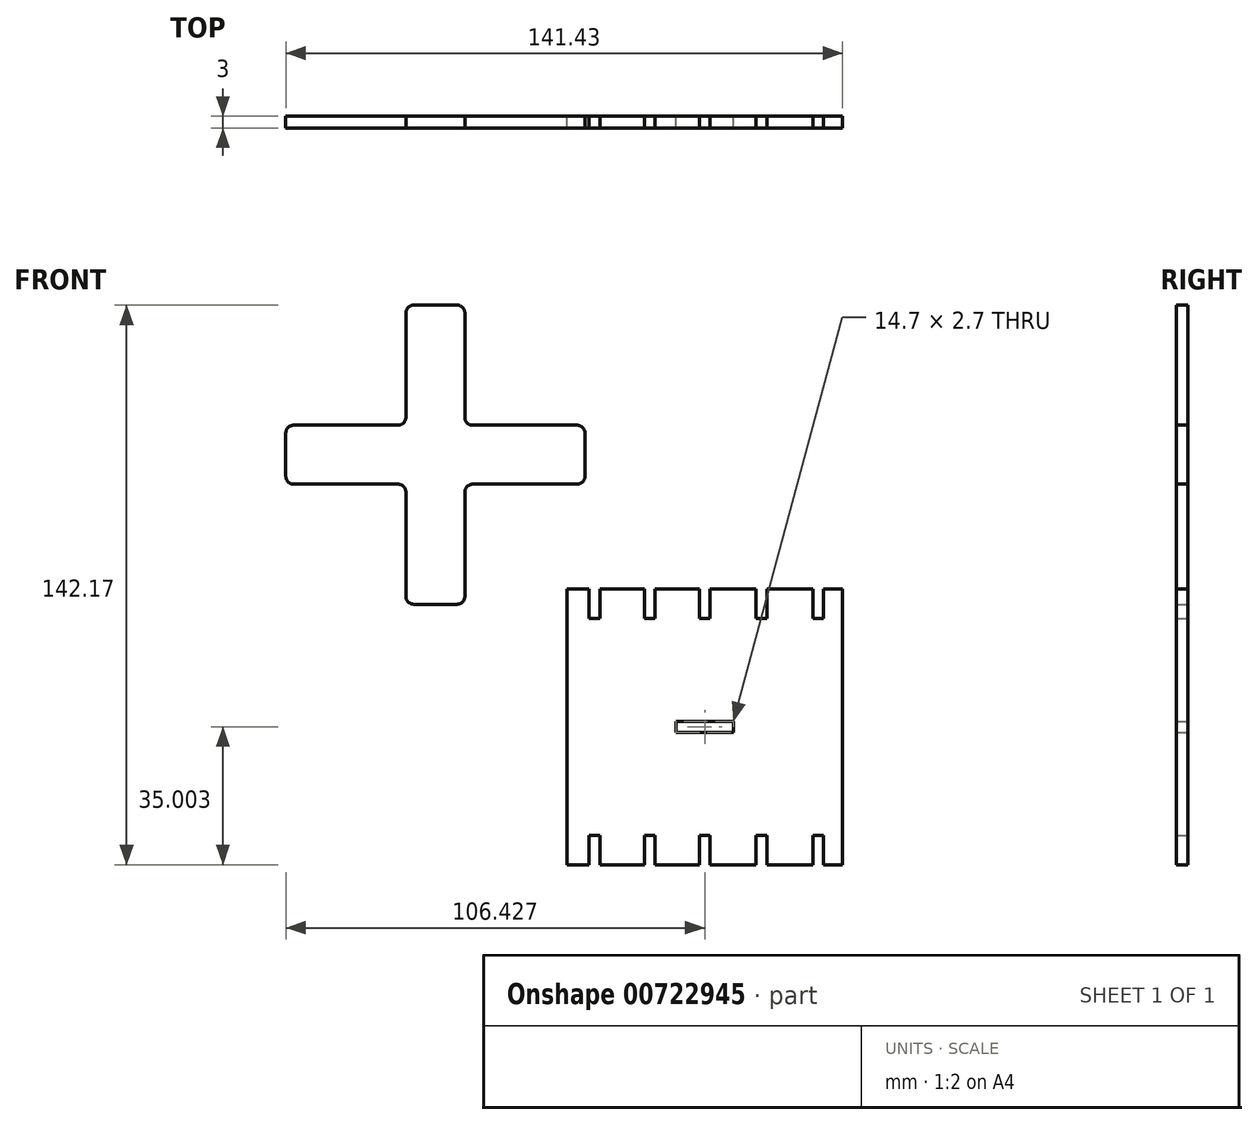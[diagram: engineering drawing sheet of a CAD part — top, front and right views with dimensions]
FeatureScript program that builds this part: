
annotation { "Feature Type Name" : "Feature", "Feature Type Description" : "" }
export const myFeature = defineFeature(function(context is Context, id is Id, definition is map)
    precondition{}
    {
        {
            var Q0;
            Q0=qCreatedBy(makeId("Front.planeOp"),FACE);
            var sketch = newSketch(context, id + "F0", { "sketchPlane" : qUnion([Q0])});
            skLineSegment(sketch, "E0.bottom", {"start": v(-54.88, 11.95) * mm, "end": v(-43.88, 11.95) * mm});
            skLineSegment(sketch, "E0.top", {"start": v(-54.88, 87.95) * mm, "end": v(-43.88, 87.95) * mm});
            skLineSegment(sketch, "E0.left", {"start": v(-56.88, 13.95) * mm, "end": v(-56.88, 40.45) * mm});
            skLineSegment(sketch, "E0.right", {"start": v(-41.88, 13.95) * mm, "end": v(-41.88, 40.45) * mm});
            skPoint(sketch, "E0.middle", {"position": v(-49.38, 49.95) * mm});
            skLineSegment(sketch, "E1.bottom", {"start": v(-13.38, 57.45) * mm, "end": v(-39.88, 57.45) * mm});
            skLineSegment(sketch, "E1.top", {"start": v(-13.38, 42.45) * mm, "end": v(-39.88, 42.45) * mm});
            skLineSegment(sketch, "E1.left", {"start": v(-11.38, 55.45) * mm, "end": v(-11.38, 44.45) * mm});
            skLineSegment(sketch, "E1.right", {"start": v(-87.38, 55.45) * mm, "end": v(-87.38, 44.45) * mm});
            skLineSegment(sketch, "E2.trimOffspring", {"start": v(-58.88, 57.45) * mm, "end": v(-85.38, 57.45) * mm});
            skLineSegment(sketch, "E3.trimOffspring", {"start": v(-41.88, 59.45) * mm, "end": v(-41.88, 85.95) * mm});
            skLineSegment(sketch, "E4.trimOffspring", {"start": v(-58.88, 42.45) * mm, "end": v(-85.38, 42.45) * mm});
            skLineSegment(sketch, "E5.trimOffspring", {"start": v(-56.88, 59.45) * mm, "end": v(-56.88, 85.95) * mm});
            skPoint(sketch, "E6.visualSharp", {"position": v(-87.38, 42.45) * mm});
            skArc(sketch, "E6.filletArc", {"start": v(-87.38, 44.45) * mm, "mid": v(-86.8, 43.04) * mm, "end": v(-85.38, 42.45) * mm});
            skPoint(sketch, "E7.visualSharp", {"position": v(-11.38, 57.45) * mm});
            skArc(sketch, "E7.filletArc", {"start": v(-11.38, 55.45) * mm, "mid": v(-11.97, 56.87) * mm, "end": v(-13.38, 57.45) * mm});
            skArc(sketch, "E8.filletArc", {"start": v(-13.38, 42.45) * mm, "mid": v(-11.97, 43.04) * mm, "end": v(-11.38, 44.45) * mm});
            skPoint(sketch, "E9.visualSharp", {"position": v(-41.88, 42.45) * mm});
            skArc(sketch, "E9.filletArc", {"start": v(-39.88, 42.45) * mm, "mid": v(-41.3, 41.87) * mm, "end": v(-41.88, 40.45) * mm});
            skPoint(sketch, "E10.visualSharp", {"position": v(-56.88, 42.45) * mm});
            skArc(sketch, "E10.filletArc", {"start": v(-56.88, 40.45) * mm, "mid": v(-57.47, 41.87) * mm, "end": v(-58.88, 42.45) * mm});
            skArc(sketch, "E11.filletArc", {"start": v(-58.88, 57.45) * mm, "mid": v(-57.47, 58.04) * mm, "end": v(-56.88, 59.45) * mm});
            skPoint(sketch, "E12.visualSharp", {"position": v(-41.88, 57.45) * mm});
            skArc(sketch, "E12.filletArc", {"start": v(-41.88, 59.45) * mm, "mid": v(-41.3, 58.04) * mm, "end": v(-39.88, 57.45) * mm});
            skPoint(sketch, "E13.visualSharp", {"position": v(-41.88, 87.95) * mm});
            skArc(sketch, "E13.filletArc", {"start": v(-41.88, 85.95) * mm, "mid": v(-42.47, 87.37) * mm, "end": v(-43.88, 87.95) * mm});
            skArc(sketch, "E14.filletArc", {"start": v(-54.88, 87.95) * mm, "mid": v(-56.3, 87.37) * mm, "end": v(-56.88, 85.95) * mm});
            skPoint(sketch, "E15.visualSharp", {"position": v(-41.88, 11.95) * mm});
            skArc(sketch, "E15.filletArc", {"start": v(-43.88, 11.95) * mm, "mid": v(-42.47, 12.54) * mm, "end": v(-41.88, 13.95) * mm});
            skPoint(sketch, "E16.visualSharp", {"position": v(-56.88, 11.95) * mm});
            skArc(sketch, "E16.filletArc", {"start": v(-56.88, 13.95) * mm, "mid": v(-56.3, 12.54) * mm, "end": v(-54.88, 11.95) * mm});
            skArc(sketch, "E17.filletArc", {"start": v(-85.38, 57.45) * mm, "mid": v(-86.8, 56.87) * mm, "end": v(-87.38, 55.45) * mm});
            skSolve(sketch);
        }
        {
            var Q0;
            Q0=qSketchRegion(id+"F0",true);
            extrude(context, id + "F1", {"entities" : qUnion([Q0]), "depth" : 3 * mm, "offsetDistance" : 25 * mm});
        }
        {
            var Q0;
            Q0=qCreatedBy(makeId("Front.planeOp"),FACE);
            var sketch = newSketch(context, id + "F2", { "sketchPlane" : qUnion([Q0])});
            skLineSegment(sketch, "E18.bottom", {"start": v(54.05, 15.78) * mm, "end": v(49.2, 15.78) * mm});
            skLineSegment(sketch, "E18.top", {"start": v(54.05, -54.22) * mm, "end": v(49.2, -54.22) * mm});
            skLineSegment(sketch, "E18.left", {"start": v(54.05, 15.78) * mm, "end": v(54.05, -54.22) * mm});
            skLineSegment(sketch, "E18.right", {"start": v(-15.95, 15.78) * mm, "end": v(-15.95, -54.22) * mm});
            skPoint(sketch, "E18.middle", {"position": v(19.05, -19.22) * mm});
            skLineSegment(sketch, "E19.top", {"start": v(20.4, 8.28) * mm, "end": v(17.7, 8.28) * mm});
            skLineSegment(sketch, "E19.left", {"start": v(20.4, 15.78) * mm, "end": v(20.4, 8.28) * mm});
            skLineSegment(sketch, "E19.right", {"start": v(17.7, 15.78) * mm, "end": v(17.7, 8.28) * mm});
            skPoint(sketch, "E19.middle", {"position": v(19.05, 15.78) * mm});
            skPoint(sketch, "E19.bottom.end.orphan", {"position": v(17.7, 23.28) * mm});
            skPoint(sketch, "E19.bottom.start.orphan", {"position": v(20.4, 23.28) * mm});
            skLineSegment(sketch, "E20.1.0.0", {"start": v(34.8, 15.78) * mm, "end": v(34.8, 8.28) * mm});
            skLineSegment(sketch, "E20.1.0.1", {"start": v(32.1, 15.78) * mm, "end": v(32.1, 8.28) * mm});
            skLineSegment(sketch, "E20.1.0.2", {"start": v(34.8, 8.28) * mm, "end": v(32.1, 8.28) * mm});
            skLineSegment(sketch, "E20.2.0.0", {"start": v(49.2, 15.78) * mm, "end": v(49.2, 8.28) * mm});
            skLineSegment(sketch, "E20.2.0.1", {"start": v(46.5, 15.78) * mm, "end": v(46.5, 8.28) * mm});
            skLineSegment(sketch, "E20.2.0.2", {"start": v(49.2, 8.28) * mm, "end": v(46.5, 8.28) * mm});
            skLineSegment(sketch, "E20.direction1", {"start": v(20.4, 8.28) * mm, "end": v(34.8, 8.28) * mm, "construction": true});
            skLineSegment(sketch, "E21.trimOffspring", {"start": v(17.7, 15.78) * mm, "end": v(6.4, 15.78) * mm});
            skLineSegment(sketch, "E22.trimOffspring", {"start": v(32.1, 15.78) * mm, "end": v(20.4, 15.78) * mm});
            skLineSegment(sketch, "E23.trimOffspring", {"start": v(46.5, 15.78) * mm, "end": v(34.8, 15.78) * mm});
            skLineSegment(sketch, "E24.1.0.0", {"start": v(3.7, 15.78) * mm, "end": v(3.7, 8.28) * mm});
            skLineSegment(sketch, "E24.1.0.1", {"start": v(6.4, 15.78) * mm, "end": v(6.4, 8.28) * mm});
            skLineSegment(sketch, "E24.1.0.2", {"start": v(6.4, 8.28) * mm, "end": v(3.7, 8.28) * mm});
            skLineSegment(sketch, "E24.2.0.0", {"start": v(-10.3, 15.78) * mm, "end": v(-10.3, 8.28) * mm});
            skLineSegment(sketch, "E24.2.0.1", {"start": v(-7.6, 15.78) * mm, "end": v(-7.6, 8.28) * mm});
            skLineSegment(sketch, "E24.2.0.2", {"start": v(-7.6, 8.28) * mm, "end": v(-10.3, 8.28) * mm});
            skLineSegment(sketch, "E24.direction1", {"start": v(17.7, 8.28) * mm, "end": v(3.7, 8.28) * mm, "construction": true});
            skLineSegment(sketch, "E25.trimOffspring", {"start": v(3.7, 15.78) * mm, "end": v(-7.6, 15.78) * mm});
            skLineSegment(sketch, "E26.trimOffspring", {"start": v(-10.3, 15.78) * mm, "end": v(-15.95, 15.78) * mm});
            skLineSegment(sketch, "E27.bottom", {"start": v(20.4, -46.72) * mm, "end": v(17.7, -46.72) * mm});
            skLineSegment(sketch, "E27.left", {"start": v(20.4, -46.72) * mm, "end": v(20.4, -54.22) * mm});
            skLineSegment(sketch, "E27.right", {"start": v(17.7, -46.72) * mm, "end": v(17.7, -54.22) * mm});
            skPoint(sketch, "E27.middle", {"position": v(19.05, -54.22) * mm});
            skPoint(sketch, "E27.top.end.orphan", {"position": v(17.7, -61.72) * mm});
            skPoint(sketch, "E27.top.start.orphan", {"position": v(20.4, -61.72) * mm});
            skLineSegment(sketch, "E28.trimOffspring", {"start": v(17.7, -54.22) * mm, "end": v(6.4, -54.22) * mm});
            skLineSegment(sketch, "E29.1.0.0", {"start": v(32.1, -46.72) * mm, "end": v(32.1, -54.22) * mm});
            skLineSegment(sketch, "E29.1.0.1", {"start": v(34.8, -46.72) * mm, "end": v(34.8, -54.22) * mm});
            skLineSegment(sketch, "E29.1.0.2", {"start": v(34.8, -46.72) * mm, "end": v(32.1, -46.72) * mm});
            skLineSegment(sketch, "E29.2.0.0", {"start": v(46.5, -46.72) * mm, "end": v(46.5, -54.22) * mm});
            skLineSegment(sketch, "E29.2.0.1", {"start": v(49.2, -46.72) * mm, "end": v(49.2, -54.22) * mm});
            skLineSegment(sketch, "E29.2.0.2", {"start": v(49.2, -46.72) * mm, "end": v(46.5, -46.72) * mm});
            skLineSegment(sketch, "E30.1.0.0", {"start": v(6.4, -46.72) * mm, "end": v(6.4, -54.22) * mm});
            skLineSegment(sketch, "E30.1.0.1", {"start": v(3.7, -46.72) * mm, "end": v(3.7, -54.22) * mm});
            skLineSegment(sketch, "E30.1.0.2", {"start": v(6.4, -46.72) * mm, "end": v(3.7, -46.72) * mm});
            skLineSegment(sketch, "E30.2.0.0", {"start": v(-7.6, -46.72) * mm, "end": v(-7.6, -54.22) * mm});
            skLineSegment(sketch, "E30.2.0.1", {"start": v(-10.3, -46.72) * mm, "end": v(-10.3, -54.22) * mm});
            skLineSegment(sketch, "E30.2.0.2", {"start": v(-7.6, -46.72) * mm, "end": v(-10.3, -46.72) * mm});
            skLineSegment(sketch, "E31.trimOffspring", {"start": v(3.7, -54.22) * mm, "end": v(-7.6, -54.22) * mm});
            skLineSegment(sketch, "E32.trimOffspring", {"start": v(-10.3, -54.22) * mm, "end": v(-15.95, -54.22) * mm});
            skLineSegment(sketch, "E33.trimOffspring", {"start": v(32.1, -54.22) * mm, "end": v(20.4, -54.22) * mm});
            skLineSegment(sketch, "E34.trimOffspring", {"start": v(20.4, -54.22) * mm, "end": v(32.1, -54.22) * mm, "construction": true});
            skLineSegment(sketch, "E35.trimOffspring", {"start": v(17.7, -54.22) * mm, "end": v(6.4, -54.22) * mm, "construction": true});
            skLineSegment(sketch, "E36.trimOffspring", {"start": v(46.5, -54.22) * mm, "end": v(34.8, -54.22) * mm});
            skLineSegment(sketch, "E37.bottom", {"start": v(26.4, -20.57) * mm, "end": v(11.7, -20.57) * mm});
            skLineSegment(sketch, "E37.top", {"start": v(26.4, -17.87) * mm, "end": v(11.7, -17.87) * mm});
            skLineSegment(sketch, "E37.left", {"start": v(26.4, -20.57) * mm, "end": v(26.4, -17.87) * mm});
            skLineSegment(sketch, "E37.right", {"start": v(11.7, -20.57) * mm, "end": v(11.7, -17.87) * mm});
            skPoint(sketch, "E38.visualSharp", {"position": v(7.66, 38.24) * mm});
            skArc(sketch, "E38.filletArc", {"start": v(7.66, 36.24) * mm, "mid": v(7.08, 37.65) * mm, "end": v(5.66, 38.24) * mm});
            skPoint(sketch, "E39.visualSharp", {"position": v(7.66, 23.24) * mm});
            skArc(sketch, "E39.filletArc", {"start": v(5.66, 23.24) * mm, "mid": v(7.08, 23.82) * mm, "end": v(7.66, 25.24) * mm});
            skPoint(sketch, "E40.visualSharp", {"position": v(-22.84, -7.26) * mm});
            skArc(sketch, "E40.filletArc", {"start": v(-24.84, -7.26) * mm, "mid": v(-23.42, -6.68) * mm, "end": v(-22.84, -5.26) * mm});
            skPoint(sketch, "E41.visualSharp", {"position": v(-37.84, -7.26) * mm});
            skArc(sketch, "E41.filletArc", {"start": v(-37.84, -5.26) * mm, "mid": v(-37.25, -6.68) * mm, "end": v(-35.84, -7.26) * mm});
            skSolve(sketch);
        }
        {
            var Q0;
            Q0 = qSketchRegion(id + "F2", true);
            extrude(context, id + "F3", {"entities" : qUnion([Q0]), "depth" : 3 * mm, "offsetDistance" : 25 * mm});
        }
    });
